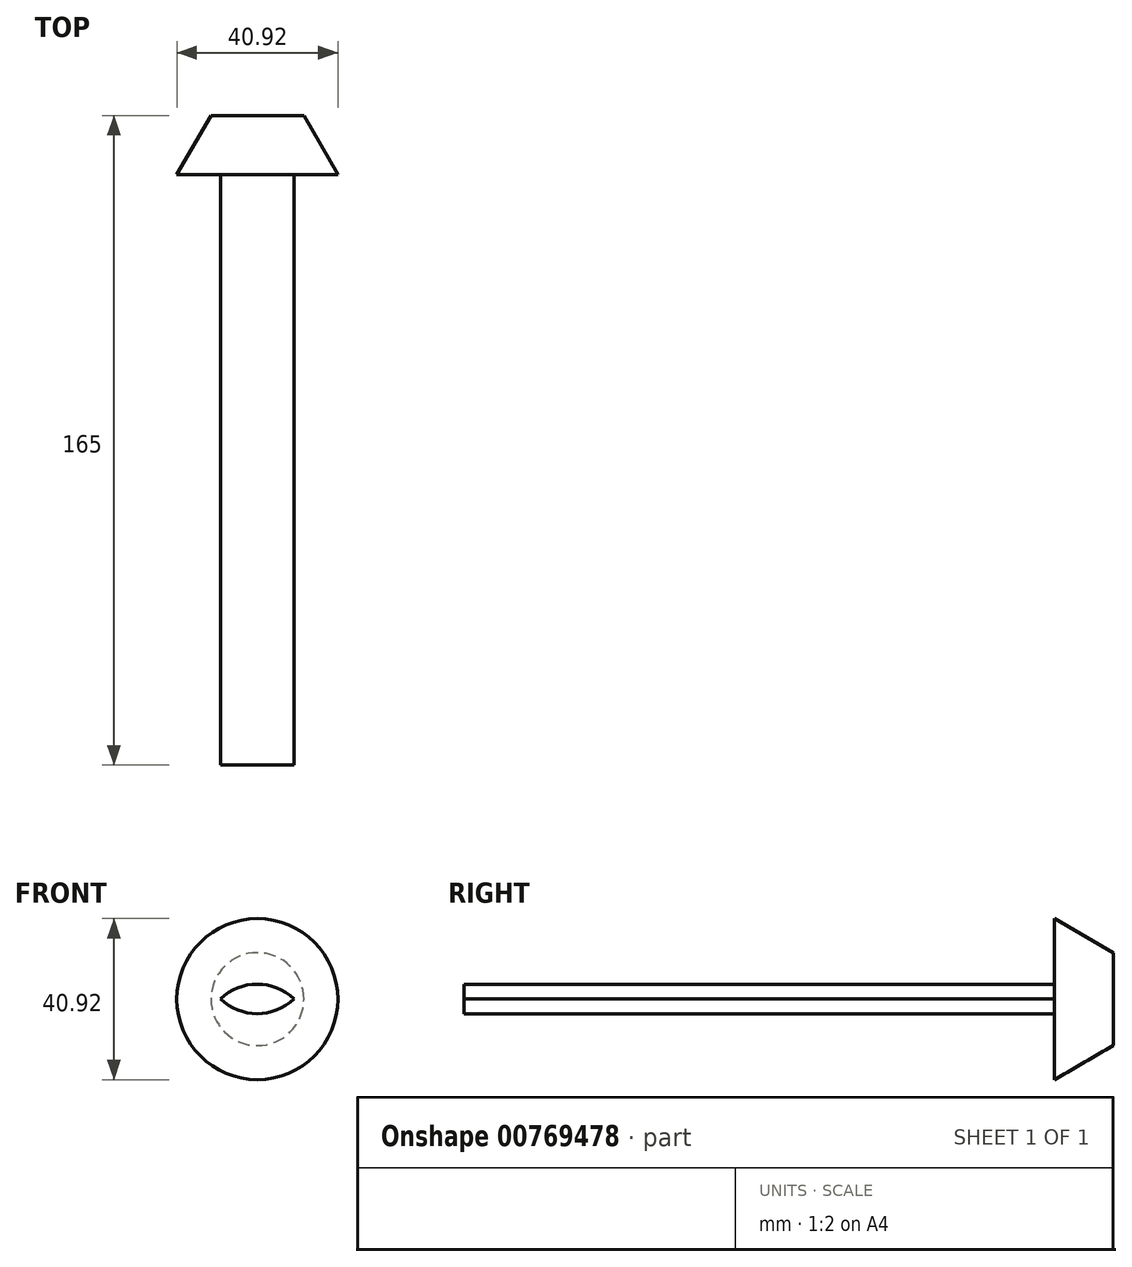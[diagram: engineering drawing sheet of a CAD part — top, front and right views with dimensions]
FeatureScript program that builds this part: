
annotation { "Feature Type Name" : "Feature", "Feature Type Description" : "" }
export const myFeature = defineFeature(function(context is Context, id is Id, definition is map)
    precondition{}
    {
        {
            var Q0;
            Q0=qCreatedBy(makeId("Front.planeOp"),FACE);
            var sketch = newSketch(context, id + "F0", { "sketchPlane" : qUnion([Q0])});
            skArc(sketch, "E0", {"start": v(-1.19, 23.42) * mm, "mid": v(-10.53, 27.17) * mm, "end": v(-19.87, 23.42) * mm});
            skArc(sketch, "E1", {"start": v(-19.87, 23.42) * mm, "mid": v(-10.53, 19.67) * mm, "end": v(-1.19, 23.42) * mm});
            skSolve(sketch);
        }
        {
            var Q0;
            Q0=makeQuery(id+"F0.imprint","IMPRINT",FACE,{"disambiguationData":[TD([[makeQuery(id+"F0.imprint","IMPRINT",EDGE,{"derivedFrom":sQuery(id+"F0.wireOp",EDGE,"E0")}),1.0]])]});
            extrude(context, id + "F1", {"entities" : qUnion([Q0]), "depth" : 165 * mm, "offsetDistance" : 25 * mm});
        }
        {
            var Q0;
            Q0=qCreatedBy(makeId("Front.planeOp"),FACE);
            var sketch = newSketch(context, id + "F2", { "sketchPlane" : qUnion([Q0])});
            skCircle(sketch, "E2", {"center": v(-10.47, 23.36) * mm, "radius": 11.8 * mm});
            skSolve(sketch);
        }
        {
            var Q0;
            Q0=makeQuery(id+"F2.imprint","IMPRINT",FACE,{"disambiguationData":[TD([[makeQuery(id+"F2.imprint","IMPRINT",EDGE,{"derivedFrom":sQuery(id+"F2.wireOp",EDGE,"E2")}),1.0]])]});
            extrude(context, id + "F3", {"entities" : qUnion([Q0]), "operationType" : NewBodyOperationType.ADD, "depth" : 15 * mm, "offsetDistance" : 25 * mm, "hasDraft" : true, "draftAngle" : 30 * degree});
        }
    });
